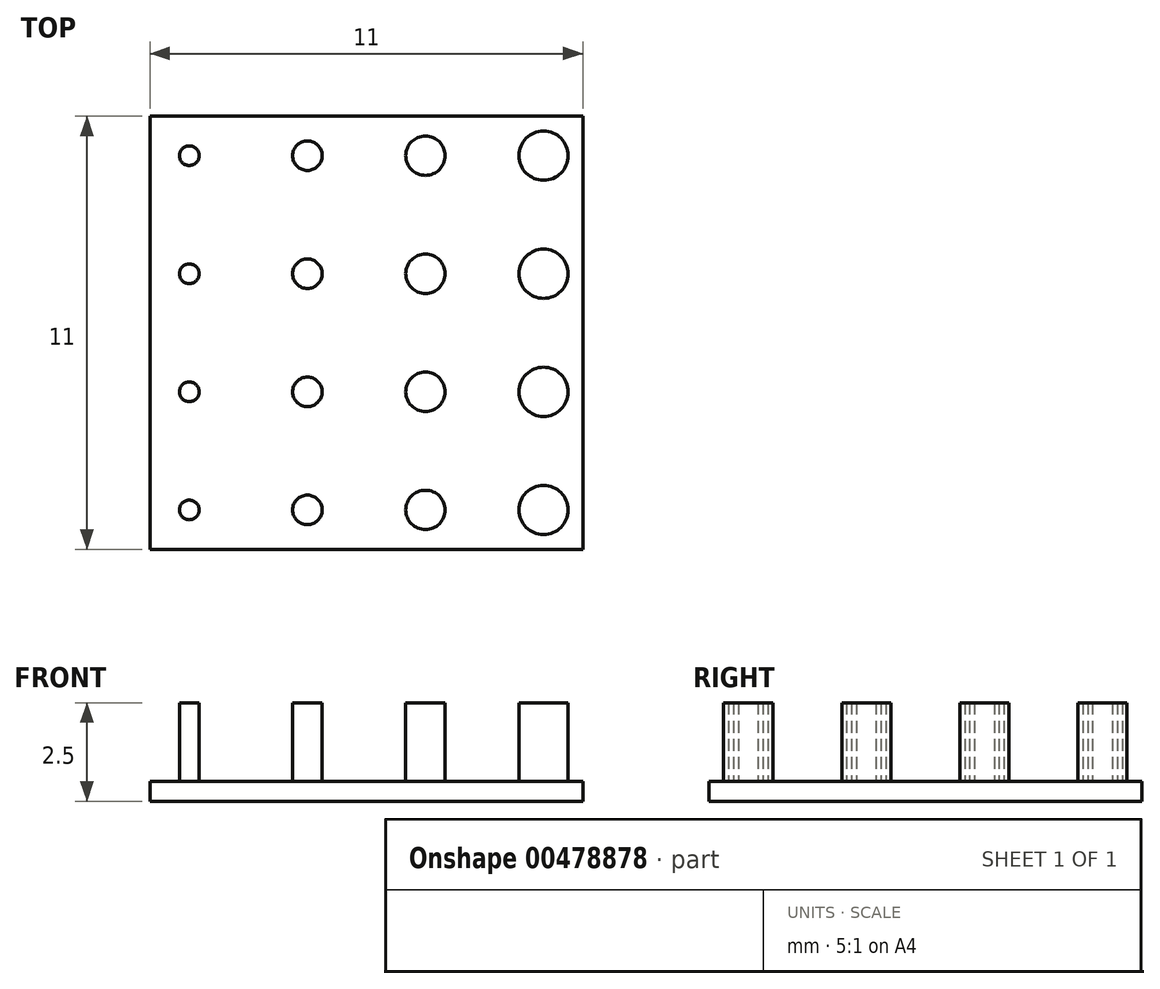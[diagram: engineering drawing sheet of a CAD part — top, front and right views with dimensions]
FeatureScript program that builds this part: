
annotation { "Feature Type Name" : "Feature", "Feature Type Description" : "" }
export const myFeature = defineFeature(function(context is Context, id is Id, definition is map)
    precondition{}
    {
        {
            var Q0;
            Q0=qCreatedBy(makeId("Top.planeOp"),FACE);
            var sketch = newSketch(context, id + "F0", { "sketchPlane" : qUnion([Q0])});
            skPoint(sketch, "E0.middle", {"position": v(0, 0) * mm});
            skPoint(sketch, "E1.1.0.0", {"position": v(-4.5, 7.5) * mm});
            skPoint(sketch, "E1.2.0.0", {"position": v(-1.5, 0) * mm});
            skPoint(sketch, "E1.3.0.0", {"position": v(1.5, 0) * mm});
            skPoint(sketch, "E1.4.0.0", {"position": v(4.5, 0) * mm});
            skLineSegment(sketch, "E1.direction1", {"start": v(-7.5, 0) * mm, "end": v(-4.5, 0) * mm, "construction": true});
            skPoint(sketch, "E2.1.0.0", {"position": v(-4.5, 4.5) * mm});
            skCircle(sketch, "E2.1.0.1", {"center": v(-1.5, 4.5) * mm, "radius": 0.38 * mm});
            skCircle(sketch, "E2.1.0.2", {"center": v(1.5, 4.5) * mm, "radius": 0.5 * mm});
            skCircle(sketch, "E2.1.0.3", {"center": v(4.5, 4.5) * mm, "radius": 0.62 * mm});
            skPoint(sketch, "E2.2.0.0", {"position": v(-4.5, 1.5) * mm});
            skCircle(sketch, "E2.2.0.1", {"center": v(-1.5, 1.5) * mm, "radius": 0.38 * mm});
            skCircle(sketch, "E2.2.0.2", {"center": v(1.5, 1.5) * mm, "radius": 0.5 * mm});
            skCircle(sketch, "E2.2.0.3", {"center": v(4.5, 1.5) * mm, "radius": 0.62 * mm});
            skPoint(sketch, "E2.3.0.0", {"position": v(-4.5, -1.5) * mm});
            skCircle(sketch, "E2.3.0.1", {"center": v(-1.5, -1.5) * mm, "radius": 0.38 * mm});
            skCircle(sketch, "E2.3.0.2", {"center": v(1.5, -1.5) * mm, "radius": 0.5 * mm});
            skCircle(sketch, "E2.3.0.3", {"center": v(4.5, -1.5) * mm, "radius": 0.62 * mm});
            skPoint(sketch, "E2.4.0.0", {"position": v(-4.5, -4.5) * mm});
            skCircle(sketch, "E2.4.0.1", {"center": v(-1.5, -4.5) * mm, "radius": 0.38 * mm});
            skCircle(sketch, "E2.4.0.2", {"center": v(1.5, -4.5) * mm, "radius": 0.5 * mm});
            skCircle(sketch, "E2.4.0.3", {"center": v(4.5, -4.5) * mm, "radius": 0.62 * mm});
            skPoint(sketch, "E2.5.0.0", {"position": v(-4.5, -7.5) * mm});
            skLineSegment(sketch, "E2.direction1", {"start": v(-4.5, 7.5) * mm, "end": v(-4.5, 4.5) * mm, "construction": true});
            skPoint(sketch, "E3.orphan", {"position": v(-7.5, 7.5) * mm});
            skPoint(sketch, "E4.orphan", {"position": v(-7.5, -7.5) * mm});
            skPoint(sketch, "E0.left.end.orphan", {"position": v(7.5, -7.5) * mm});
            skPoint(sketch, "E0.left.start.orphan", {"position": v(7.5, 7.5) * mm});
            skCircle(sketch, "E5", {"center": v(-4.5, 4.5) * mm, "radius": 0.25 * mm});
            skCircle(sketch, "E6", {"center": v(-4.5, 1.5) * mm, "radius": 0.25 * mm});
            skCircle(sketch, "E7", {"center": v(-4.5, -1.5) * mm, "radius": 0.25 * mm});
            skCircle(sketch, "E8", {"center": v(-4.5, -4.5) * mm, "radius": 0.25 * mm});
            skSolve(sketch);
        }
        {
            var Q0;
            Q0 = qSketchRegion(id + "F0", true);
            extrude(context, id + "F1", {"entities" : qUnion([Q0]), "depth" : 2 * mm});
        }
        {
            var Q0;
            Q0=qCreatedBy(makeId("Top.planeOp"),FACE);
            var sketch = newSketch(context, id + "F2", { "sketchPlane" : qUnion([Q0])});
            skLineSegment(sketch, "E9.bottom", {"start": v(5.5, 5.5) * mm, "end": v(-5.5, 5.5) * mm});
            skLineSegment(sketch, "E9.top", {"start": v(5.5, -5.5) * mm, "end": v(-5.5, -5.5) * mm});
            skLineSegment(sketch, "E9.left", {"start": v(5.5, 5.5) * mm, "end": v(5.5, -5.5) * mm});
            skLineSegment(sketch, "E9.right", {"start": v(-5.5, 5.5) * mm, "end": v(-5.5, -5.5) * mm});
            skPoint(sketch, "E9.middle", {"position": v(0, 0) * mm});
            skSolve(sketch);
        }
        {
            var Q0;
            Q0 = qSketchRegion(id + "F2", true);
            extrude(context, id + "F3", {"entities" : qUnion([Q0]), "oppositeDirection" : true, "depth" : .5 * mm});
        }
    });
